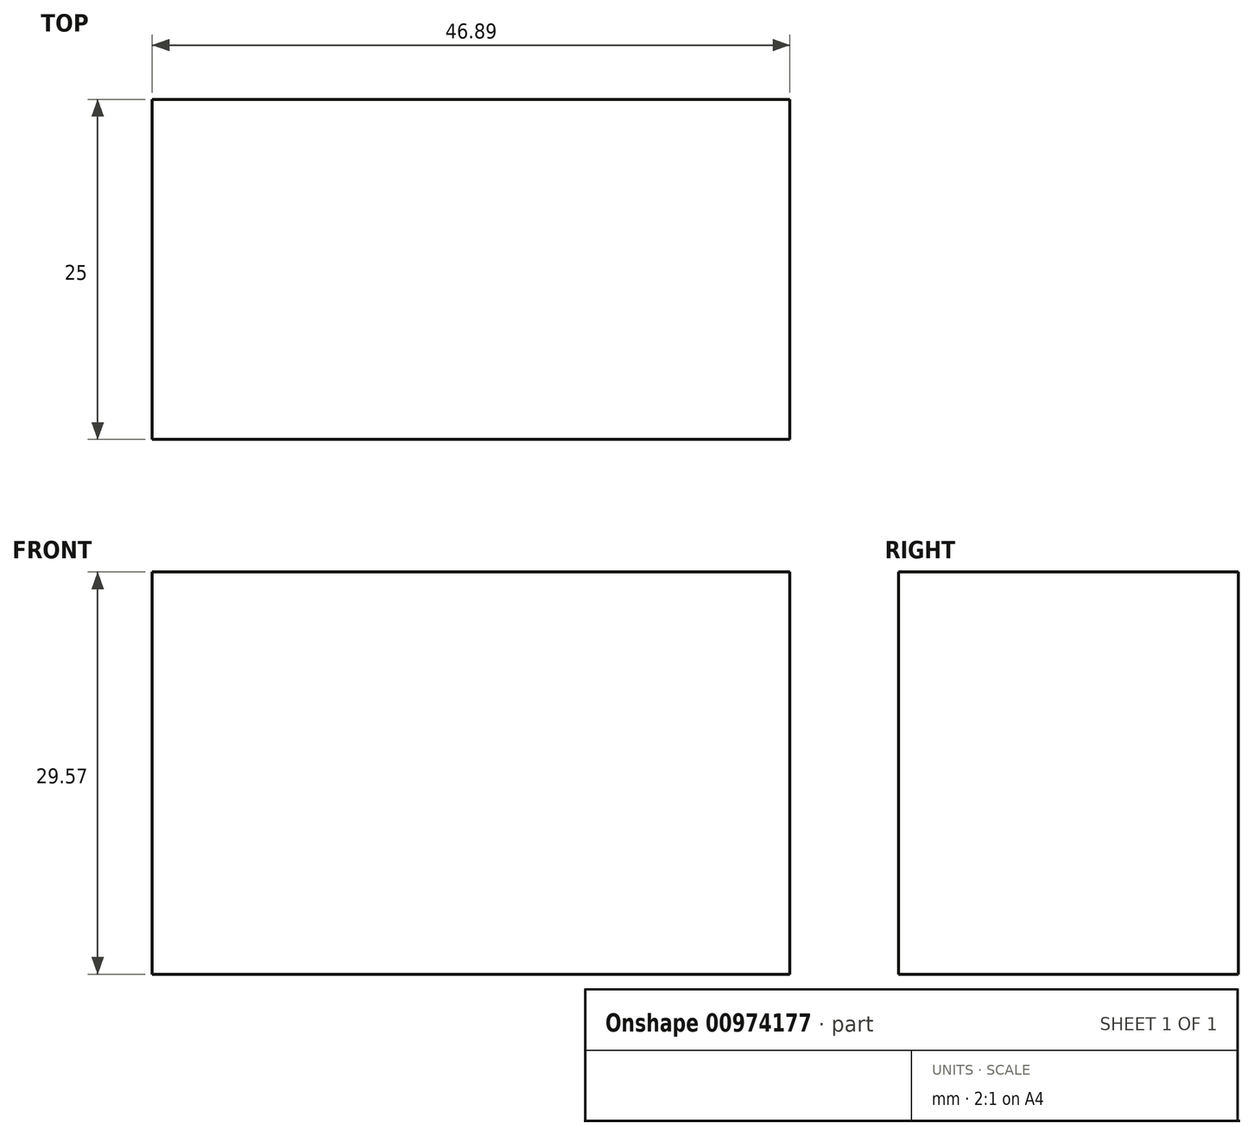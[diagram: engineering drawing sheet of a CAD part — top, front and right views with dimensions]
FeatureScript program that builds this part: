
annotation { "Feature Type Name" : "Feature", "Feature Type Description" : "" }
export const myFeature = defineFeature(function(context is Context, id is Id, definition is map)
    precondition{}
    {
        {
            var Q0;
            Q0=qCreatedBy(makeId("Front.planeOp"),FACE);
            var sketch = newSketch(context, id + "F0", { "sketchPlane" : qUnion([Q0])});
            skLineSegment(sketch, "E0.bottom", {"start": v(-61.84, 35.37) * mm, "end": v(-14.95, 35.37) * mm});
            skLineSegment(sketch, "E0.top", {"start": v(-61.84, 5.8) * mm, "end": v(-14.95, 5.8) * mm});
            skLineSegment(sketch, "E0.left", {"start": v(-61.84, 35.37) * mm, "end": v(-61.84, 5.8) * mm});
            skLineSegment(sketch, "E0.right", {"start": v(-14.95, 35.37) * mm, "end": v(-14.95, 5.8) * mm});
            skSolve(sketch);
        }
        {
            var Q0;
            Q0 = qSketchRegion(id + "F0", true);
            extrude(context, id + "F1", {"entities" : qUnion([Q0]), "depth" : 25 * mm, "offsetDistance" : 25 * mm});
        }
    });
